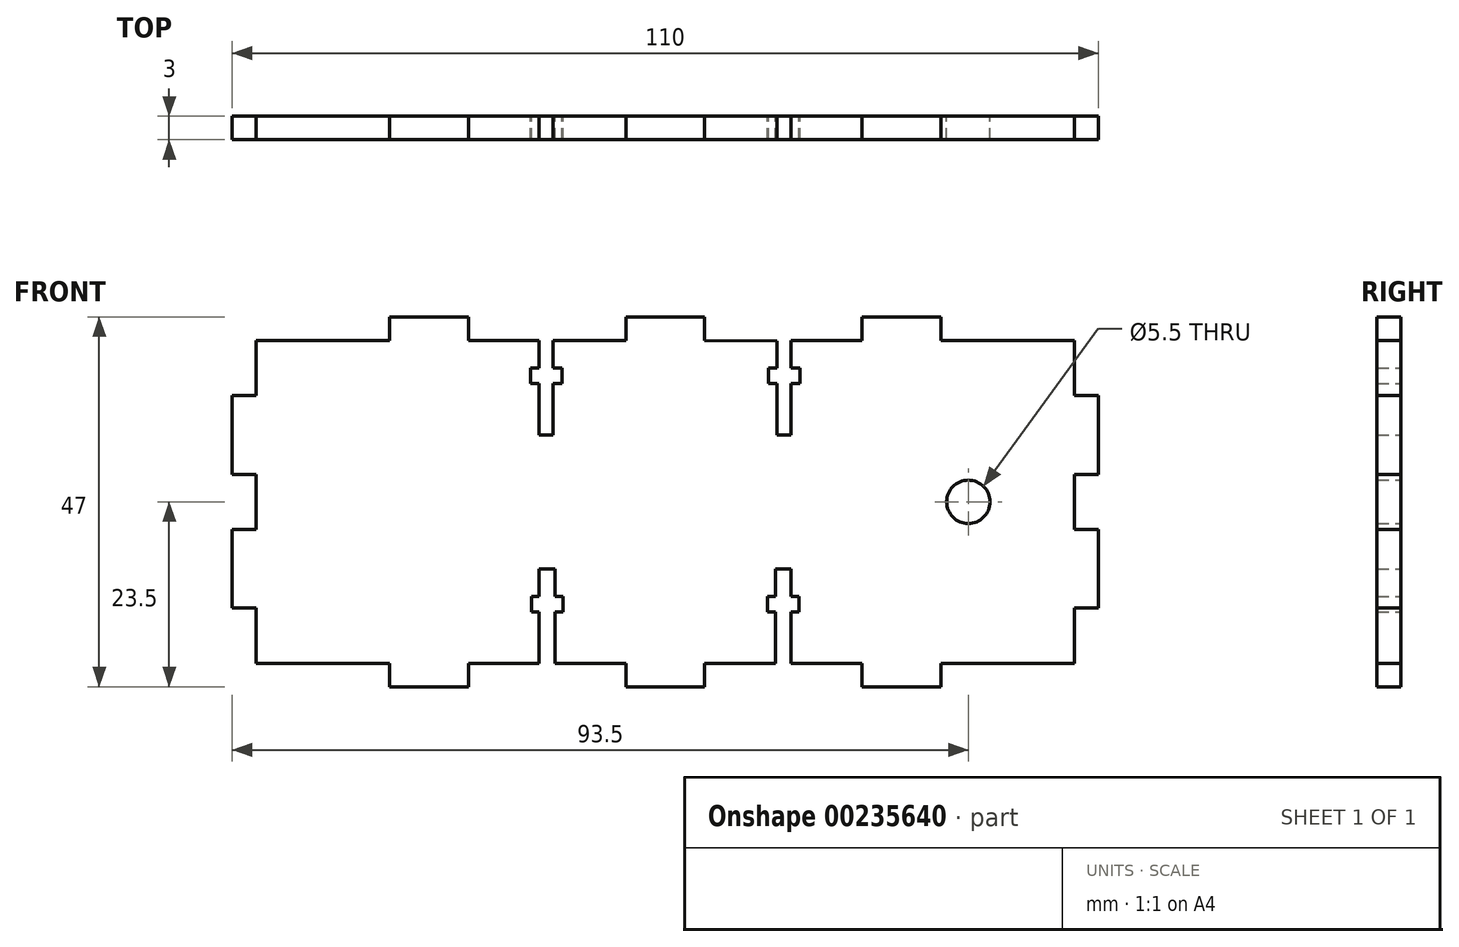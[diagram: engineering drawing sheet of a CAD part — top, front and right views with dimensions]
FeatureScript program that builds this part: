
annotation { "Feature Type Name" : "Feature", "Feature Type Description" : "" }
export const myFeature = defineFeature(function(context is Context, id is Id, definition is map)
    precondition{}
    {
        {
            var Q0;
            Q0=qCreatedBy(makeId("Front.planeOp"),FACE);
            var sketch = newSketch(context, id + "F0", { "sketchPlane" : qUnion([Q0])});
            skLineSegment(sketch, "E0", {"start": v(0, 0) * mm, "end": v(0, 7) * mm});
            skLineSegment(sketch, "E1", {"start": v(0, 7) * mm, "end": v(3, 7) * mm});
            skLineSegment(sketch, "E2", {"start": v(3, 7) * mm, "end": v(3, 17) * mm});
            skLineSegment(sketch, "E3", {"start": v(3, 17) * mm, "end": v(0, 17) * mm});
            skLineSegment(sketch, "E4", {"start": v(0, 17) * mm, "end": v(0, 24) * mm});
            skLineSegment(sketch, "E5", {"start": v(0, 24) * mm, "end": v(3, 24) * mm});
            skLineSegment(sketch, "E6", {"start": v(3, 24) * mm, "end": v(3, 34) * mm});
            skLineSegment(sketch, "E7", {"start": v(3, 34) * mm, "end": v(0, 34) * mm});
            skLineSegment(sketch, "E8", {"start": v(0, 34) * mm, "end": v(0, 41) * mm});
            skLineSegment(sketch, "E9", {"start": v(0, 41) * mm, "end": v(-17, 41) * mm});
            skLineSegment(sketch, "E10", {"start": v(-17, 41) * mm, "end": v(-17, 44) * mm});
            skLineSegment(sketch, "E11", {"start": v(-27, 44) * mm, "end": v(-27, 41) * mm});
            skLineSegment(sketch, "E12", {"start": v(-47, 41) * mm, "end": v(-47, 44) * mm});
            skLineSegment(sketch, "E13", {"start": v(0, 0) * mm, "end": v(-17, 0) * mm});
            skLineSegment(sketch, "E14", {"start": v(-17, 0) * mm, "end": v(-17, -3) * mm});
            skLineSegment(sketch, "E15", {"start": v(-27, -3) * mm, "end": v(-27, 0) * mm});
            skLineSegment(sketch, "E16", {"start": v(-27, 0) * mm, "end": v(-36, 0) * mm});
            skLineSegment(sketch, "E17", {"start": v(-47, 0) * mm, "end": v(-47, -3) * mm});
            skLineSegment(sketch, "E18.MirrorCS", {"start": v(-57, 41) * mm, "end": v(-57, 44) * mm});
            skLineSegment(sketch, "E19.MirrorCS", {"start": v(-104, 7) * mm, "end": v(-107, 7) * mm});
            skLineSegment(sketch, "E20.MirrorCS", {"start": v(-87, 0) * mm, "end": v(-87, -3) * mm});
            skLineSegment(sketch, "E21.MirrorCS", {"start": v(-107, 17) * mm, "end": v(-104, 17) * mm});
            skLineSegment(sketch, "E22.MirrorCS", {"start": v(-77, -3) * mm, "end": v(-77, 0) * mm});
            skLineSegment(sketch, "E23.MirrorCS", {"start": v(-104, 24) * mm, "end": v(-107, 24) * mm});
            skLineSegment(sketch, "E24.MirrorCS", {"start": v(-107, 34) * mm, "end": v(-104, 34) * mm});
            skLineSegment(sketch, "E25.MirrorCS", {"start": v(-87, 41) * mm, "end": v(-87, 44) * mm});
            skLineSegment(sketch, "E26.MirrorCS", {"start": v(-77, 44) * mm, "end": v(-77, 41) * mm});
            skLineSegment(sketch, "E27.MirrorCS", {"start": v(-57, 0) * mm, "end": v(-57, -3) * mm});
            skLineSegment(sketch, "E28.MirrorCS", {"start": v(-104, 0) * mm, "end": v(-87, 0) * mm});
            skLineSegment(sketch, "E29.MirrorCS", {"start": v(-104, 0) * mm, "end": v(-104, 7) * mm});
            skLineSegment(sketch, "E30.MirrorCS", {"start": v(-77, 41) * mm, "end": v(-68, 41) * mm});
            skLineSegment(sketch, "E31.MirrorCS", {"start": v(-107, 7) * mm, "end": v(-107, 17) * mm});
            skLineSegment(sketch, "E32.MirrorCS", {"start": v(-87, -3) * mm, "end": v(-77, -3) * mm});
            skLineSegment(sketch, "E33.MirrorCS", {"start": v(-77, 0) * mm, "end": v(-68, 0) * mm});
            skLineSegment(sketch, "E34.MirrorCS", {"start": v(-104, 17) * mm, "end": v(-104, 24) * mm});
            skLineSegment(sketch, "E35.MirrorCS", {"start": v(-107, 24) * mm, "end": v(-107, 34) * mm});
            skLineSegment(sketch, "E36.MirrorCS", {"start": v(-104, 34) * mm, "end": v(-104, 41) * mm});
            skLineSegment(sketch, "E37.MirrorCS", {"start": v(-104, 41) * mm, "end": v(-87, 41) * mm});
            skLineSegment(sketch, "E38.MirrorCS", {"start": v(-87, 44) * mm, "end": v(-77, 44) * mm});
            skPoint(sketch, "E39.centerSnap0", {"position": v(0, 20.5) * mm});
            skPoint(sketch, "E39.centerSnap1", {"position": v(-8.5, 0) * mm});
            skLineSegment(sketch, "E40.top", {"start": v(-68, 29) * mm, "end": v(-66.22, 29) * mm});
            skLineSegment(sketch, "E41", {"start": v(-57, -3) * mm, "end": v(-47, -3) * mm});
            skLineSegment(sketch, "E42", {"start": v(-17, -3) * mm, "end": v(-27, -3) * mm});
            skLineSegment(sketch, "E43", {"start": v(-57, 44) * mm, "end": v(-47, 44) * mm});
            skLineSegment(sketch, "E44.trimOffspring", {"start": v(-66.22, 41) * mm, "end": v(-57, 41) * mm});
            skLineSegment(sketch, "E45.MirrorCS", {"start": v(-69, 8.5) * mm, "end": v(-68, 8.5) * mm});
            skLineSegment(sketch, "E46.MirrorCS", {"start": v(-69, 6.5) * mm, "end": v(-68, 6.5) * mm});
            skLineSegment(sketch, "E47.MirrorCS", {"start": v(-65, 6.5) * mm, "end": v(-65, 8.5) * mm});
            skLineSegment(sketch, "E48.MirrorCS", {"start": v(-66, 8.5) * mm, "end": v(-65, 8.5) * mm});
            skLineSegment(sketch, "E49.MirrorCS", {"start": v(-68, 12) * mm, "end": v(-66, 12) * mm});
            skLineSegment(sketch, "E50.MirrorCS", {"start": v(-66, 6.5) * mm, "end": v(-65, 6.5) * mm});
            skLineSegment(sketch, "E51.MirrorCS", {"start": v(-66, 8.5) * mm, "end": v(-66, 12) * mm});
            skLineSegment(sketch, "E52.MirrorCS", {"start": v(-68, 8.5) * mm, "end": v(-68, 12) * mm});
            skLineSegment(sketch, "E53.MirrorCS", {"start": v(-68, 0) * mm, "end": v(-68, 6.5) * mm});
            skLineSegment(sketch, "E54.MirrorCS", {"start": v(-66, 0) * mm, "end": v(-66, 6.5) * mm});
            skLineSegment(sketch, "E55", {"start": v(-27, 44) * mm, "end": v(-17, 44) * mm});
            skLineSegment(sketch, "E56.MirrorCS", {"start": v(-39, 6.5) * mm, "end": v(-39, 8.5) * mm});
            skLineSegment(sketch, "E57.MirrorCS", {"start": v(-38, 6.5) * mm, "end": v(-39, 6.5) * mm});
            skLineSegment(sketch, "E58.MirrorCS", {"start": v(-35, 6.5) * mm, "end": v(-36, 6.5) * mm});
            skLineSegment(sketch, "E59.MirrorCS", {"start": v(-38, 8.5) * mm, "end": v(-39, 8.5) * mm});
            skLineSegment(sketch, "E60.MirrorCS", {"start": v(-36, 12) * mm, "end": v(-38, 12) * mm});
            skLineSegment(sketch, "E61.MirrorCS", {"start": v(-35, 8.5) * mm, "end": v(-36, 8.5) * mm});
            skLineSegment(sketch, "E62.MirrorCS", {"start": v(-38, 8.5) * mm, "end": v(-38, 12) * mm});
            skLineSegment(sketch, "E63.MirrorCS", {"start": v(-36, 8.5) * mm, "end": v(-36, 12) * mm});
            skLineSegment(sketch, "E64.MirrorCS", {"start": v(-36, 0) * mm, "end": v(-36, 6.5) * mm});
            skLineSegment(sketch, "E65.MirrorCS", {"start": v(-38, 0) * mm, "end": v(-38, 6.5) * mm});
            skLineSegment(sketch, "E66.trimOffspring", {"start": v(-66, 0) * mm, "end": v(-57, 0) * mm});
            skLineSegment(sketch, "E67.trimOffspring", {"start": v(-38, 0) * mm, "end": v(-47, 0) * mm});
            skLineSegment(sketch, "E68", {"start": v(-68, 41) * mm, "end": v(-68, 37.5) * mm});
            skLineSegment(sketch, "E69", {"start": v(-66.22, 41) * mm, "end": v(-66.22, 37.5) * mm});
            skLineSegment(sketch, "E70.bottom", {"start": v(-69.1, 37.5) * mm, "end": v(-68, 37.5) * mm});
            skLineSegment(sketch, "E70.top", {"start": v(-69.1, 35.5) * mm, "end": v(-68, 35.5) * mm});
            skLineSegment(sketch, "E70.left", {"start": v(-69.1, 37.5) * mm, "end": v(-69.1, 35.5) * mm});
            skLineSegment(sketch, "E70.right", {"start": v(-65.1, 37.5) * mm, "end": v(-65.1, 35.5) * mm});
            skLineSegment(sketch, "E71.trimOffspring", {"start": v(-68, 35.5) * mm, "end": v(-68, 29) * mm});
            skLineSegment(sketch, "E72.trimOffspring", {"start": v(-66.22, 35.5) * mm, "end": v(-66.22, 29) * mm});
            skLineSegment(sketch, "E73.trimOffspring", {"start": v(-66.22, 35.5) * mm, "end": v(-65.1, 35.5) * mm});
            skLineSegment(sketch, "E74.trimOffspring", {"start": v(-66.22, 37.5) * mm, "end": v(-65.1, 37.5) * mm});
            skLineSegment(sketch, "E75.MirrorCS", {"start": v(-34.9, 35.5) * mm, "end": v(-36, 35.5) * mm});
            skLineSegment(sketch, "E76.MirrorCS", {"start": v(-34.9, 37.5) * mm, "end": v(-36, 37.5) * mm});
            skLineSegment(sketch, "E77.MirrorCS", {"start": v(-37.78, 37.5) * mm, "end": v(-38.9, 37.5) * mm});
            skLineSegment(sketch, "E78.MirrorCS", {"start": v(-37.78, 35.5) * mm, "end": v(-38.9, 35.5) * mm});
            skLineSegment(sketch, "E79.MirrorCS", {"start": v(-36, 29) * mm, "end": v(-37.78, 29) * mm});
            skLineSegment(sketch, "E80.MirrorCS", {"start": v(-36, 35.5) * mm, "end": v(-36, 29) * mm});
            skLineSegment(sketch, "E81.MirrorCS", {"start": v(-38.9, 37.5) * mm, "end": v(-38.9, 35.5) * mm});
            skLineSegment(sketch, "E82.MirrorCS", {"start": v(-37.78, 35.5) * mm, "end": v(-37.78, 29) * mm});
            skLineSegment(sketch, "E83.MirrorCS", {"start": v(-34.9, 37.5) * mm, "end": v(-34.9, 35.5) * mm});
            skLineSegment(sketch, "E84.MirrorCS", {"start": v(-36, 41) * mm, "end": v(-36, 37.5) * mm});
            skLineSegment(sketch, "E85", {"start": v(-35, 6.5) * mm, "end": v(-35, 8.5) * mm});
            skLineSegment(sketch, "E86", {"start": v(-69, 8.5) * mm, "end": v(-69, 6.5) * mm});
            skLineSegment(sketch, "E87", {"start": v(-37.78, 37.5) * mm, "end": v(-37.78, 40.92) * mm});
            skLineSegment(sketch, "E88", {"start": v(-27, 41) * mm, "end": v(-36, 41) * mm});
            skLineSegment(sketch, "E89", {"start": v(-47, 41) * mm, "end": v(-37.78, 40.92) * mm});
            skCircle(sketch, "E90", {"center": v(-13.5, 20.5) * mm, "radius": 2.75 * mm});
            skSolve(sketch);
        }
        {
            var Q0;
            Q0 = qSketchRegion(id + "F0", true);
            extrude(context, id + "F1", {"entities" : qUnion([Q0]), "depth" : 3 * mm});
        }
    });
